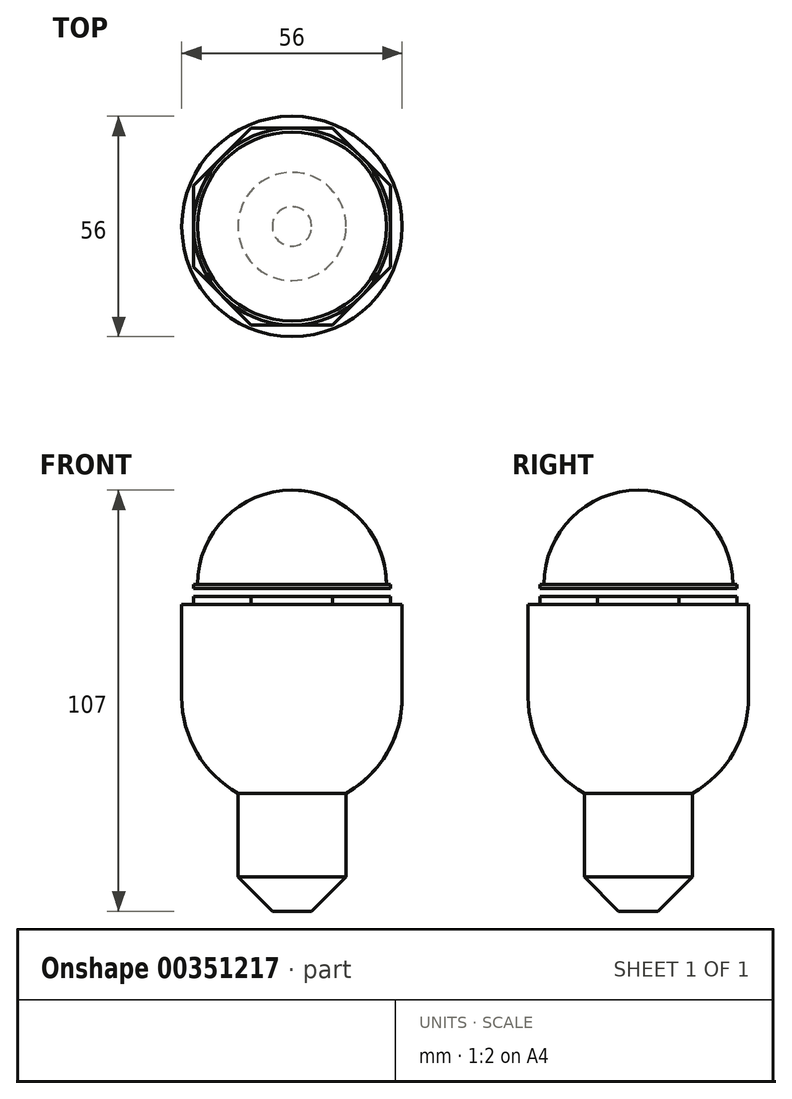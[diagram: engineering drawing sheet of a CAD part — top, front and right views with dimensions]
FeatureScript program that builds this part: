
annotation { "Feature Type Name" : "Feature", "Feature Type Description" : "" }
export const myFeature = defineFeature(function(context is Context, id is Id, definition is map)
    precondition{}
    {
        {
            var Q0;
            Q0=qCreatedBy(makeId("Front.planeOp"),FACE);
            var sketch = newSketch(context, id + "F0", { "sketchPlane" : qUnion([Q0])});
            skLineSegment(sketch, "E0", {"start": v(0, 0) * mm, "end": v(25, 0) * mm});
            skLineSegment(sketch, "E1", {"start": v(25, 0) * mm, "end": v(25, 1) * mm});
            skLineSegment(sketch, "E2", {"start": v(25, 1) * mm, "end": v(24, 1) * mm});
            skArc(sketch, "E3", {"start": v(24, 1) * mm, "mid": v(16.97, 17.97) * mm, "end": v(0, 25) * mm});
            skLineSegment(sketch, "E4", {"start": v(0, 25) * mm, "end": v(0, 1) * mm});
            skLineSegment(sketch, "E5", {"start": v(0, 1) * mm, "end": v(0, 0) * mm});
            skLineSegment(sketch, "E6", {"start": v(0, -4) * mm, "end": v(28, -4) * mm});
            skLineSegment(sketch, "E7", {"start": v(28, -4) * mm, "end": v(28, -27.6) * mm});
            skLineSegment(sketch, "E8", {"start": v(13.75, -52) * mm, "end": v(13.75, -56.33) * mm});
            skLineSegment(sketch, "E9", {"start": v(13.75, -56.33) * mm, "end": v(13.75, -73.25) * mm});
            skLineSegment(sketch, "E10", {"start": v(13.75, -73.25) * mm, "end": v(5, -82) * mm});
            skLineSegment(sketch, "E11", {"start": v(5, -82) * mm, "end": v(0, -82) * mm});
            skLineSegment(sketch, "E12", {"start": v(0, -82) * mm, "end": v(0, -4) * mm});
            skArc(sketch, "E13.filletArc", {"start": v(13.75, -52) * mm, "mid": v(24.18, -41.73) * mm, "end": v(28, -27.6) * mm});
            skSolve(sketch);
        }
        {
            var Q0;
            Q0=makeQuery(id+"F0.imprint","IMPRINT",FACE,{"disambiguationData":[TD([[makeQuery(id+"F0.imprint","IMPRINT",EDGE,{"derivedFrom":sQuery(id+"F0.wireOp",EDGE,"E0")}),1.0]])]});
            var Q1;
            Q1=makeQuery(id+"F0.imprint","IMPRINT",FACE,{"disambiguationData":[TD([[makeQuery(id+"F0.imprint","IMPRINT",EDGE,{"derivedFrom":sQuery(id+"F0.wireOp",EDGE,"E6")}),-1.0]])]});
            var Q2;
            Q2=sQuery(id+"F0.wireOp",EDGE,"E4");
            revolve(context, id + "F1", {"entities" : qUnion([Q0, Q1]), "axis" : qUnion([Q2]), "revolveType" : RevolveType.FULL});
        }
        {
            var Q0;
            Q0=makeQuery(id+"F1.opRevolve","SWEPT_FACE",FACE,{"disambiguationData":[OSD([sQuery(id+"F0.wireOp",EDGE,"E6")])]});
            var sketch = newSketch(context, id + "F2", { "sketchPlane" : qUnion([Q0])});
            skCircle(sketch, "E14.cCircle", {"center": v(0, 0) * mm, "radius": 25 * mm, "construction": true});
            skLineSegment(sketch, "E14.0", {"start": v(-10.36, 25) * mm, "end": v(10.36, 25) * mm});
            skLineSegment(sketch, "E14.1", {"start": v(10.36, 25) * mm, "end": v(25, 10.36) * mm});
            skLineSegment(sketch, "E14.2", {"start": v(25, 10.36) * mm, "end": v(25, -10.36) * mm});
            skLineSegment(sketch, "E14.3", {"start": v(25, -10.36) * mm, "end": v(10.36, -25) * mm});
            skLineSegment(sketch, "E14.4", {"start": v(10.36, -25) * mm, "end": v(-10.36, -25) * mm});
            skLineSegment(sketch, "E14.5", {"start": v(-10.36, -25) * mm, "end": v(-25, -10.36) * mm});
            skLineSegment(sketch, "E14.6", {"start": v(-25, -10.36) * mm, "end": v(-25, 10.36) * mm});
            skLineSegment(sketch, "E14.7", {"start": v(-25, 10.36) * mm, "end": v(-10.36, 25) * mm});
            skPoint(sketch, "E14.0.midPoint", {"position": v(0, 25) * mm});
            skSolve(sketch);
        }
        {
            var Q0;
            Q0 = qSketchRegion(id + "F2", true);
            extrude(context, id + "F3", {"entities" : qUnion([Q0]), "operationType" : NewBodyOperationType.ADD, "depth" : 2 * mm});
        }
    });
